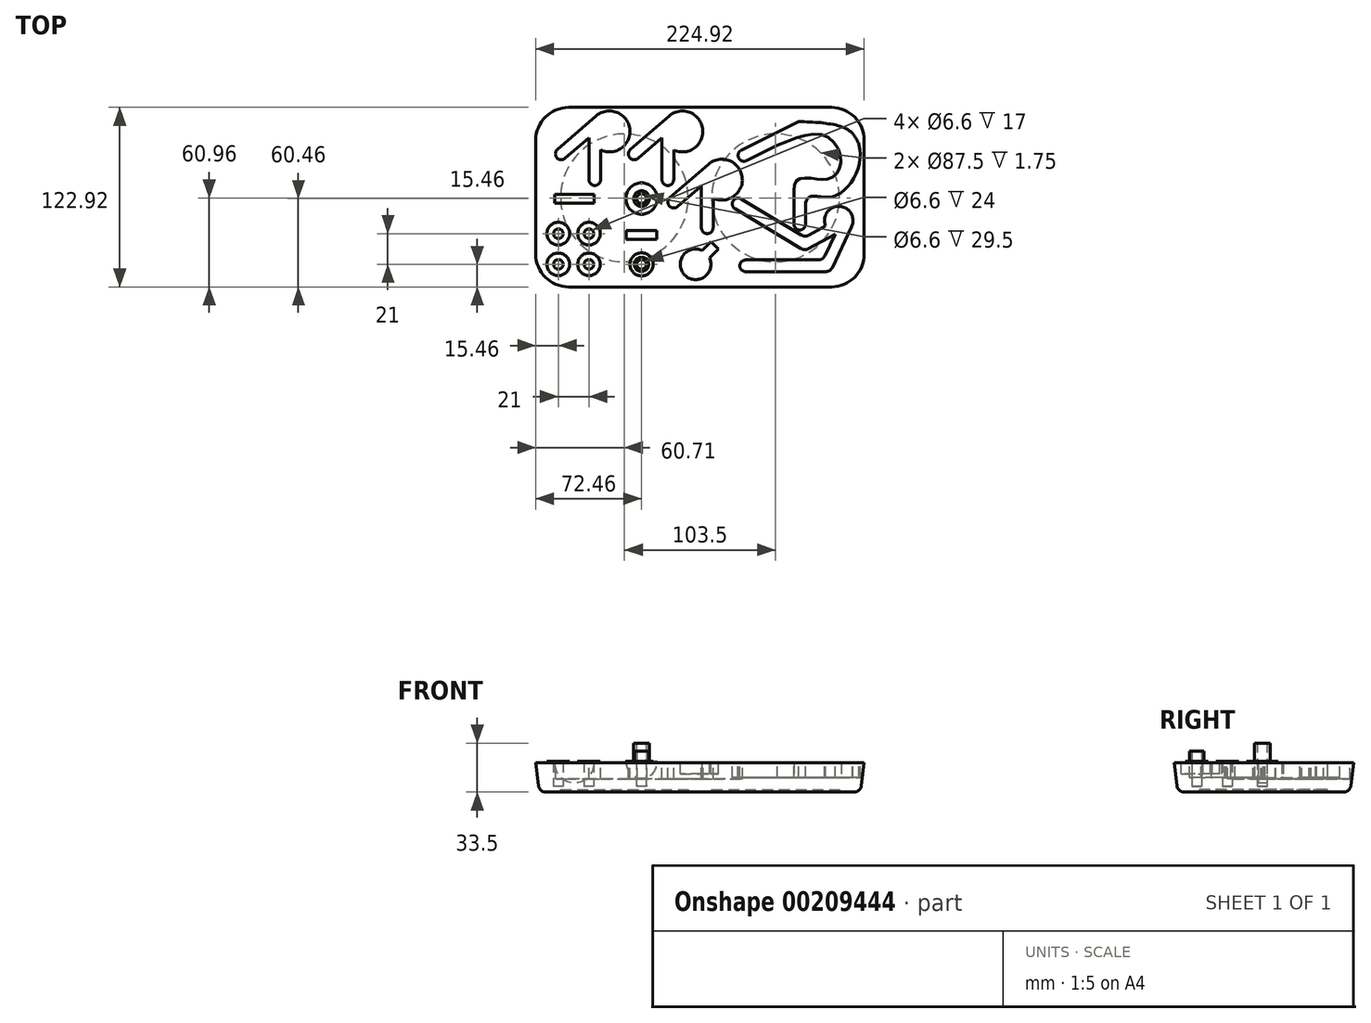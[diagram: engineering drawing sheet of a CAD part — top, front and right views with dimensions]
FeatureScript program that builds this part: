
annotation { "Feature Type Name" : "Feature", "Feature Type Description" : "" }
export const myFeature = defineFeature(function(context is Context, id is Id, definition is map)
    precondition{}
    {
        {
            var Q0;
            Q0=qCreatedBy(makeId("Top.planeOp"),FACE);
            var sketch = newSketch(context, id + "F0", { "sketchPlane" : qUnion([Q0])});
            skLineSegment(sketch, "E0.bottom", {"start": v(20, 0) * mm, "end": v(200, 0) * mm});
            skLineSegment(sketch, "E0.top", {"start": v(20, 118) * mm, "end": v(200, 118) * mm});
            skLineSegment(sketch, "E0.left", {"start": v(0, 20) * mm, "end": v(0, 98) * mm});
            skLineSegment(sketch, "E0.right", {"start": v(220, 20) * mm, "end": v(220, 98) * mm});
            skPoint(sketch, "E1.visualSharp", {"position": v(0, 118) * mm});
            skArc(sketch, "E1.filletArc", {"start": v(20, 118) * mm, "mid": v(5.86, 112.14) * mm, "end": v(0, 98) * mm});
            skPoint(sketch, "E2.visualSharp", {"position": v(220, 118) * mm});
            skArc(sketch, "E2.filletArc", {"start": v(220, 98) * mm, "mid": v(214.14, 112.14) * mm, "end": v(200, 118) * mm});
            skPoint(sketch, "E3.visualSharp", {"position": v(0, 0) * mm});
            skArc(sketch, "E3.filletArc", {"start": v(0, 20) * mm, "mid": v(5.86, 5.86) * mm, "end": v(20, 0) * mm});
            skPoint(sketch, "E4.visualSharp", {"position": v(220, 0) * mm});
            skArc(sketch, "E4.filletArc", {"start": v(200, 0) * mm, "mid": v(214.14, 5.86) * mm, "end": v(220, 20) * mm});
            skSolve(sketch);
        }
        {
            var Q0;
            Q0=makeQuery(id+"F0.imprint","IMPRINT",FACE,{"disambiguationData":[TD([[makeQuery(id+"F0.imprint","IMPRINT",EDGE,{"derivedFrom":sQuery(id+"F0.wireOp",EDGE,"E0.bottom")}),1.0]])]});
            extrude(context, id + "F1", {"entities" : qUnion([Q0]), "depth" : 20 * mm, "hasDraft" : true, "draftAngle" : 7 * degree});
        }
        {
            var Q0;
            Q0=makeQuery(id+"F1.opExtrude","CAP_FACE",FACE,{"disambiguationData":[OSD([sQuery(id+"F0.wireOp",EDGE,"E0.bottom"),sQuery(id+"F0.wireOp",EDGE,"E0.top"),sQuery(id+"F0.wireOp",EDGE,"E0.left"),sQuery(id+"F0.wireOp",EDGE,"E0.right"),sQuery(id+"F0.wireOp",EDGE,"E1.filletArc"),sQuery(id+"F0.wireOp",EDGE,"E2.filletArc"),sQuery(id+"F0.wireOp",EDGE,"E3.filletArc"),sQuery(id+"F0.wireOp",EDGE,"E4.filletArc")])],"isStart":true});
            fillet(context, id + "F2", {"entities" : qUnion([Q0]), "radius" : 5 * mm, "tangentPropagation" : true, "allowEdgeOverflow" : false});
        }
        {
            var Q0;
            Q0=makeQuery(id+"F1.opExtrude","CAP_FACE",FACE,{"disambiguationData":[OSD([sQuery(id+"F0.wireOp",EDGE,"E0.bottom"),sQuery(id+"F0.wireOp",EDGE,"E0.top"),sQuery(id+"F0.wireOp",EDGE,"E0.left"),sQuery(id+"F0.wireOp",EDGE,"E0.right"),sQuery(id+"F0.wireOp",EDGE,"E1.filletArc"),sQuery(id+"F0.wireOp",EDGE,"E2.filletArc"),sQuery(id+"F0.wireOp",EDGE,"E3.filletArc"),sQuery(id+"F0.wireOp",EDGE,"E4.filletArc")])],"isStart":true});
            var sketch = newSketch(context, id + "F3", { "sketchPlane" : qUnion([Q0])});
            skLineSegment(sketch, "E5.bottom", {"start": v(0, 0) * mm, "end": v(58.25, 0) * mm, "construction": true});
            skLineSegment(sketch, "E5.top", {"start": v(0, -58.5) * mm, "end": v(58.25, -58.5) * mm, "construction": true});
            skLineSegment(sketch, "E5.left", {"start": v(0, 0) * mm, "end": v(0, -58.5) * mm, "construction": true});
            skLineSegment(sketch, "E5.right", {"start": v(58.25, 0) * mm, "end": v(58.25, -58.5) * mm, "construction": true});
            skLineSegment(sketch, "E6.bottom", {"start": v(0, 0) * mm, "end": v(161.75, 0) * mm, "construction": true});
            skLineSegment(sketch, "E6.top", {"start": v(0, -58.5) * mm, "end": v(161.75, -58.5) * mm, "construction": true});
            skLineSegment(sketch, "E6.right", {"start": v(161.75, 0) * mm, "end": v(161.75, -58.5) * mm, "construction": true});
            skCircle(sketch, "E7", {"center": v(58.25, -58.5) * mm, "radius": 43.75 * mm});
            skCircle(sketch, "E8", {"center": v(161.75, -58.5) * mm, "radius": 43.75 * mm});
            skSolve(sketch);
        }
        {
            var Q0;
            Q0=qSketchRegion(id+"F3",true);
            extrude(context, id + "F4", {"entities" : qUnion([Q0]), "operationType" : NewBodyOperationType.REMOVE, "oppositeDirection" : true, "depth" : 1.75 * mm});
        }
        {
            var Q0;
            Q0=makeQuery(id+"F1.opExtrude","CAP_FACE",FACE,{"disambiguationData":[OSD([sQuery(id+"F0.wireOp",EDGE,"E0.bottom"),sQuery(id+"F0.wireOp",EDGE,"E0.top"),sQuery(id+"F0.wireOp",EDGE,"E0.left"),sQuery(id+"F0.wireOp",EDGE,"E0.right"),sQuery(id+"F0.wireOp",EDGE,"E1.filletArc"),sQuery(id+"F0.wireOp",EDGE,"E2.filletArc"),sQuery(id+"F0.wireOp",EDGE,"E3.filletArc"),sQuery(id+"F0.wireOp",EDGE,"E4.filletArc")])],"isStart":false});
            var sketch = newSketch(context, id + "F5", { "sketchPlane" : qUnion([Q0])});
            skLineSegment(sketch, "E9.bottom", {"start": v(0, 0) * mm, "end": v(205, 0) * mm, "construction": true});
            skLineSegment(sketch, "E9.top", {"start": v(0, 43) * mm, "end": v(205, 43) * mm, "construction": true});
            skLineSegment(sketch, "E9.left", {"start": v(0, 0) * mm, "end": v(0, 43) * mm, "construction": true});
            skLineSegment(sketch, "E9.right", {"start": v(205, 0) * mm, "end": v(205, 43) * mm, "construction": true});
            skArc(sketch, "E10", {"start": v(213.81, 38.83) * mm, "mid": v(205.19, 52.75) * mm, "end": v(196.03, 39.18) * mm});
            skLineSegment(sketch, "E11", {"start": v(213.81, 38.83) * mm, "end": v(200.6, 10.86) * mm});
            skLineSegment(sketch, "E12", {"start": v(196.07, 8) * mm, "end": v(141.24, 8) * mm});
            skLineSegment(sketch, "E13", {"start": v(137.24, 12) * mm, "end": v(137.24, 12) * mm});
            skLineSegment(sketch, "E14", {"start": v(141.24, 16) * mm, "end": v(191, 16) * mm});
            skPoint(sketch, "E15.visualSharp", {"position": v(194.17, 16) * mm});
            skArc(sketch, "E15.filletArc", {"start": v(191, 16) * mm, "mid": v(193.68, 16.78) * mm, "end": v(195.53, 18.86) * mm});
            skPoint(sketch, "E16.visualSharp", {"position": v(199.24, 8) * mm});
            skArc(sketch, "E16.filletArc", {"start": v(196.07, 8) * mm, "mid": v(198.75, 8.78) * mm, "end": v(200.6, 10.86) * mm});
            skPoint(sketch, "E17.visualSharp", {"position": v(137.24, 16) * mm});
            skArc(sketch, "E17.filletArc", {"start": v(141.24, 16) * mm, "mid": v(138.41, 14.83) * mm, "end": v(137.24, 12) * mm});
            skPoint(sketch, "E18.visualSharp", {"position": v(137.24, 8) * mm});
            skArc(sketch, "E18.filletArc", {"start": v(137.24, 12) * mm, "mid": v(138.41, 9.17) * mm, "end": v(141.24, 8) * mm});
            skLineSegment(sketch, "E19.trimOffspring", {"start": v(202.48, 33.58) * mm, "end": v(195.53, 18.86) * mm});
            skLineSegment(sketch, "E20", {"start": v(196.03, 39.18) * mm, "end": v(184.43, 32.88) * mm});
            skLineSegment(sketch, "E21", {"start": v(179.46, 32.99) * mm, "end": v(138.25, 57.86) * mm});
            skLineSegment(sketch, "E22", {"start": v(132.76, 56.5) * mm, "end": v(132.76, 56.5) * mm});
            skLineSegment(sketch, "E23", {"start": v(134.12, 51.01) * mm, "end": v(179.25, 23.77) * mm});
            skLineSegment(sketch, "E24", {"start": v(202.48, 33.58) * mm, "end": v(184.22, 23.66) * mm});
            skPoint(sketch, "E25.visualSharp", {"position": v(181.7, 22.3) * mm});
            skArc(sketch, "E25.filletArc", {"start": v(179.25, 23.77) * mm, "mid": v(181.72, 23.05) * mm, "end": v(184.22, 23.66) * mm});
            skPoint(sketch, "E26.visualSharp", {"position": v(181.91, 31.5) * mm});
            skArc(sketch, "E26.filletArc", {"start": v(179.46, 32.99) * mm, "mid": v(181.93, 32.27) * mm, "end": v(184.43, 32.88) * mm});
            skPoint(sketch, "E27.visualSharp", {"position": v(134.82, 59.93) * mm});
            skArc(sketch, "E27.filletArc", {"start": v(138.25, 57.86) * mm, "mid": v(135.22, 58.32) * mm, "end": v(132.76, 56.5) * mm});
            skPoint(sketch, "E28.visualSharp", {"position": v(130.7, 53.08) * mm});
            skArc(sketch, "E28.filletArc", {"start": v(132.76, 56.5) * mm, "mid": v(132.3, 53.48) * mm, "end": v(134.12, 51.01) * mm});
            skLineSegment(sketch, "E29.bottom", {"start": v(0, 0) * mm, "end": v(191, 0) * mm, "construction": true});
            skLineSegment(sketch, "E29.top", {"start": v(0, 84) * mm, "end": v(191, 84) * mm, "construction": true});
            skLineSegment(sketch, "E29.left", {"start": v(0, 0) * mm, "end": v(0, 84) * mm, "construction": true});
            skLineSegment(sketch, "E29.right", {"start": v(191, 0) * mm, "end": v(191, 84) * mm, "construction": true});
            skLineSegment(sketch, "E30", {"start": v(177.57, 110.83) * mm, "end": v(138.3, 91.17) * mm});
            skLineSegment(sketch, "E31", {"start": v(136.52, 85.8) * mm, "end": v(136.52, 85.8) * mm});
            skLineSegment(sketch, "E32", {"start": v(141.88, 84.01) * mm, "end": v(162.91, 94.54) * mm});
            skPoint(sketch, "E33.visualSharp", {"position": v(174.15, 39.17) * mm});
            skPoint(sketch, "E34.visualSharp", {"position": v(182.15, 39.17) * mm});
            skPoint(sketch, "E35.visualSharp", {"position": v(138.3, 82.22) * mm});
            skArc(sketch, "E35.filletArc", {"start": v(136.52, 85.8) * mm, "mid": v(138.83, 83.8) * mm, "end": v(141.88, 84.01) * mm});
            skPoint(sketch, "E36.visualSharp", {"position": v(134.73, 89.38) * mm});
            skArc(sketch, "E36.filletArc", {"start": v(138.3, 91.17) * mm, "mid": v(136.3, 88.85) * mm, "end": v(136.52, 85.8) * mm});
            skArc(sketch, "E37", {"start": v(174.32, 40.48) * mm, "mid": v(178.32, 36.48) * mm, "end": v(182.32, 40.48) * mm});
            skLineSegment(sketch, "E38", {"start": v(182.32, 55.28) * mm, "end": v(182.32, 40.48) * mm});
            skLineSegment(sketch, "E39", {"start": v(174.32, 59.6) * mm, "end": v(174.32, 40.48) * mm});
            skFitSpline(sketch, "E40", {"points": [v(174.32, 59.6) * mm, v(176.31, 70.54) * mm, v(187.5, 71.78) * mm, v(199.68, 72.28) * mm, v(206.63, 83.7) * mm, v(195.45, 101.1) * mm, v(162.91, 94.54) * mm], "startDerivative": vector(-2.68, 96.5) * mm, "endDerivative": vector(-150.94, -63.2) * mm});
            skFitSpline(sketch, "E41", {"points": [v(182.32, 55.28) * mm, v(185.68, 59.44) * mm, v(200.84, 59.44) * mm, v(218.24, 78.83) * mm, v(214.35, 102.83) * mm, v(177.57, 110.83) * mm], "startDerivative": vector(21.88, 51.8) * mm, "endDerivative": vector(-161.72, 6.15) * mm});
            skArc(sketch, "E42.trimOffspring", {"start": v(218.92, 94.98) * mm, "mid": v(201.73, 112.01) * mm, "end": v(177.57, 110.83) * mm});
            skSolve(sketch);
        }
        {
            var Q0;
            Q0=makeQuery(id+"F5.imprint","IMPRINT",FACE,{"disambiguationData":[TD([[makeQuery(id+"F5.imprint","IMPRINT",EDGE,{"derivedFrom":sQuery(id+"F5.wireOp",EDGE,"E30")}),1.0]])]});
            var Q1;
            Q1=makeQuery(id+"F5.imprint","IMPRINT",FACE,{"disambiguationData":[TD([[makeQuery(id+"F5.imprint","IMPRINT",EDGE,{"derivedFrom":sQuery(id+"F5.wireOp",EDGE,"E10")}),1.0]])]});
            extrude(context, id + "F6", {"entities" : qUnion([Q0, Q1]), "operationType" : NewBodyOperationType.REMOVE, "oppositeDirection" : true, "depth" : 10 * mm});
        }
        {
            var Q0;
            Q0=makeQuery(id+"F1.opExtrude","CAP_FACE",FACE,{"disambiguationData":[OSD([sQuery(id+"F0.wireOp",EDGE,"E0.bottom"),sQuery(id+"F0.wireOp",EDGE,"E0.top"),sQuery(id+"F0.wireOp",EDGE,"E0.left"),sQuery(id+"F0.wireOp",EDGE,"E0.right"),sQuery(id+"F0.wireOp",EDGE,"E1.filletArc"),sQuery(id+"F0.wireOp",EDGE,"E2.filletArc"),sQuery(id+"F0.wireOp",EDGE,"E3.filletArc"),sQuery(id+"F0.wireOp",EDGE,"E4.filletArc")])],"isStart":false});
            var sketch = newSketch(context, id + "F7", { "sketchPlane" : qUnion([Q0])});
            skLineSegment(sketch, "E43.bottom", {"start": v(0, 0) * mm, "end": v(13, 0) * mm, "construction": true});
            skLineSegment(sketch, "E43.top", {"start": v(0, 13) * mm, "end": v(13, 13) * mm, "construction": true});
            skLineSegment(sketch, "E43.left", {"start": v(0, 0) * mm, "end": v(0, 13) * mm, "construction": true});
            skLineSegment(sketch, "E43.right", {"start": v(13, 0) * mm, "end": v(13, 13) * mm, "construction": true});
            skLineSegment(sketch, "E44.bottom", {"start": v(13, 13) * mm, "end": v(34, 13) * mm, "construction": true});
            skLineSegment(sketch, "E44.top", {"start": v(13, 34) * mm, "end": v(34, 34) * mm, "construction": true});
            skLineSegment(sketch, "E44.left", {"start": v(13, 13) * mm, "end": v(13, 34) * mm, "construction": true});
            skLineSegment(sketch, "E44.right", {"start": v(34, 13) * mm, "end": v(34, 34) * mm, "construction": true});
            skCircle(sketch, "E45", {"center": v(13, 34) * mm, "radius": 7.75 * mm});
            skCircle(sketch, "E46", {"center": v(34, 34) * mm, "radius": 7.75 * mm});
            skCircle(sketch, "E47", {"center": v(34, 13) * mm, "radius": 7.75 * mm});
            skCircle(sketch, "E48", {"center": v(13, 13) * mm, "radius": 7.75 * mm});
            skCircle(sketch, "E49", {"center": v(34, 34) * mm, "radius": 3.3 * mm});
            skCircle(sketch, "E50", {"center": v(34, 13) * mm, "radius": 3.3 * mm});
            skCircle(sketch, "E51", {"center": v(13, 13) * mm, "radius": 3.3 * mm});
            skCircle(sketch, "E52", {"center": v(13, 34) * mm, "radius": 3.3 * mm});
            skSolve(sketch);
        }
        {
            var Q0;
            Q0 = qSketchRegion(id + "F7", true);
            extrude(context, id + "F8", {"entities" : qUnion([Q0]), "operationType" : NewBodyOperationType.ADD, "depth" : 1 * mm});
        }
        {
            var Q0;
            Q0=makeQuery(id+"F7.imprint","IMPRINT",FACE,{"disambiguationData":[TD([[makeQuery(id+"F7.imprint","IMPRINT",EDGE,{"derivedFrom":sQuery(id+"F7.wireOp",EDGE,"E52")}),1.0]])]});
            var Q1;
            Q1=makeQuery(id+"F7.imprint","IMPRINT",FACE,{"disambiguationData":[TD([[makeQuery(id+"F7.imprint","IMPRINT",EDGE,{"derivedFrom":sQuery(id+"F7.wireOp",EDGE,"E49")}),1.0]])]});
            var Q2;
            Q2=makeQuery(id+"F7.imprint","IMPRINT",FACE,{"disambiguationData":[TD([[makeQuery(id+"F7.imprint","IMPRINT",EDGE,{"derivedFrom":sQuery(id+"F7.wireOp",EDGE,"E50")}),1.0]])]});
            var Q3;
            Q3=makeQuery(id+"F7.imprint","IMPRINT",FACE,{"disambiguationData":[TD([[makeQuery(id+"F7.imprint","IMPRINT",EDGE,{"derivedFrom":sQuery(id+"F7.wireOp",EDGE,"E51")}),1.0]])]});
            extrude(context, id + "F9", {"entities" : qUnion([Q0, Q1, Q2, Q3]), "operationType" : NewBodyOperationType.REMOVE, "oppositeDirection" : true, "depth" : 16 * mm});
        }
        {
            var Q0;
            {var subQ0=sQuery(id+"F0.wireOp",EDGE,"E0.bottom");var subQ1=sQuery(id+"F0.wireOp",EDGE,"E2.filletArc");var subQ2=sQuery(id+"F0.wireOp",EDGE,"E0.right");var subQ3=sQuery(id+"F0.wireOp",EDGE,"E0.left");var subQ4=sQuery(id+"F0.wireOp",EDGE,"E0.top");var subQ5=sQuery(id+"F0.wireOp",EDGE,"E1.filletArc");var subQ6=sQuery(id+"F0.wireOp",EDGE,"E3.filletArc");var subQ7=sQuery(id+"F0.wireOp",EDGE,"E4.filletArc");Q0=makeQuery(id+"F8.boolean.opBoolean","SPLIT",FACE,{"disambiguationData":[TD([makeQuery(id+"F1.opExtrude","SWEPT_FACE",FACE,{"disambiguationData":[OSD([subQ0])]})])],"derivedFrom":makeQuery(id+"F1.opExtrude","CAP_FACE",FACE,{"disambiguationData":[OSD([subQ0,subQ4,subQ3,subQ2,subQ5,subQ1,subQ6,subQ7])],"isStart":false})});}
            var sketch = newSketch(context, id + "F10", { "sketchPlane" : qUnion([Q0])});
            skLineSegment(sketch, "E53.bottom", {"start": v(0, 0) * mm, "end": v(24, 0) * mm, "construction": true});
            skLineSegment(sketch, "E53.top", {"start": v(0, 55) * mm, "end": v(24, 55) * mm, "construction": true});
            skLineSegment(sketch, "E53.left", {"start": v(0, 0) * mm, "end": v(0, 55) * mm, "construction": true});
            skLineSegment(sketch, "E53.right", {"start": v(24, 0) * mm, "end": v(24, 55) * mm, "construction": true});
            skLineSegment(sketch, "E54.bottom", {"start": v(24, 55) * mm, "end": v(37.5, 55) * mm});
            skLineSegment(sketch, "E54.top", {"start": v(24, 61) * mm, "end": v(37.5, 61) * mm});
            skLineSegment(sketch, "E54.left", {"start": v(24, 55) * mm, "end": v(24, 61) * mm});
            skLineSegment(sketch, "E54.right", {"start": v(37.5, 55) * mm, "end": v(37.5, 61) * mm});
            skSolve(sketch);
        }
        {
            var Q0;
            Q0=makeQuery(id+"F10.imprint","IMPRINT",FACE,{"disambiguationData":[TD([[makeQuery(id+"F10.imprint","IMPRINT",EDGE,{"derivedFrom":sQuery(id+"F10.wireOp",EDGE,"E54.bottom")}),1.0]])]});
            var Q1;
            Q1=sQuery(id+"F10.wireOp",EDGE,"E54.left");
            revolve(context, id + "F11", {"operationType" : NewBodyOperationType.REMOVE, "entities" : qUnion([Q0]), "axis" : qUnion([Q1]), "revolveType" : RevolveType.FULL, "oppositeDirection" : true});
        }
        {
            var Q0;
            {var subQ0=sQuery(id+"F0.wireOp",EDGE,"E0.bottom");var subQ1=sQuery(id+"F0.wireOp",EDGE,"E2.filletArc");var subQ2=sQuery(id+"F0.wireOp",EDGE,"E0.right");var subQ3=sQuery(id+"F0.wireOp",EDGE,"E0.left");var subQ4=sQuery(id+"F0.wireOp",EDGE,"E0.top");var subQ5=sQuery(id+"F0.wireOp",EDGE,"E1.filletArc");var subQ6=sQuery(id+"F0.wireOp",EDGE,"E3.filletArc");var subQ7=sQuery(id+"F0.wireOp",EDGE,"E4.filletArc");Q0=makeQuery(id+"F8.boolean.opBoolean","SPLIT",FACE,{"disambiguationData":[TD([makeQuery(id+"F1.opExtrude","SWEPT_FACE",FACE,{"disambiguationData":[OSD([subQ0])]})])],"derivedFrom":makeQuery(id+"F1.opExtrude","CAP_FACE",FACE,{"disambiguationData":[OSD([subQ0,subQ4,subQ3,subQ2,subQ5,subQ1,subQ6,subQ7])],"isStart":false})});}
            var sketch = newSketch(context, id + "F12", { "sketchPlane" : qUnion([Q0])});
            skLineSegment(sketch, "E55.bottom", {"start": v(0, 0) * mm, "end": v(70, 0) * mm, "construction": true});
            skLineSegment(sketch, "E55.top", {"start": v(0, 58) * mm, "end": v(70, 58) * mm, "construction": true});
            skLineSegment(sketch, "E55.left", {"start": v(0, 0) * mm, "end": v(0, 58) * mm, "construction": true});
            skLineSegment(sketch, "E55.right", {"start": v(70, 0) * mm, "end": v(70, 58) * mm, "construction": true});
            skCircle(sketch, "E56", {"center": v(70, 58) * mm, "radius": 5.35 * mm});
            skCircle(sketch, "E57", {"center": v(70, 58) * mm, "radius": 3.3 * mm});
            skCircle(sketch, "E58", {"center": v(70, 58) * mm, "radius": 10.75 * mm});
            skLineSegment(sketch, "E59.top", {"start": v(0, 13) * mm, "end": v(70, 13) * mm, "construction": true});
            skLineSegment(sketch, "E59.left", {"start": v(0, 0) * mm, "end": v(0, 13) * mm, "construction": true});
            skLineSegment(sketch, "E59.right", {"start": v(70, 0) * mm, "end": v(70, 13) * mm, "construction": true});
            skCircle(sketch, "E60", {"center": v(70, 13) * mm, "radius": 3.3 * mm});
            skCircle(sketch, "E61", {"center": v(70, 13) * mm, "radius": 7.9 * mm});
            skCircle(sketch, "E62", {"center": v(70, 13) * mm, "radius": 4.9 * mm});
            skSolve(sketch);
        }
        {
            var Q0;
            Q0=makeQuery(id+"F12.imprint","IMPRINT",FACE,{"disambiguationData":[TD([[makeQuery(id+"F12.imprint","IMPRINT",EDGE,{"derivedFrom":sQuery(id+"F12.wireOp",EDGE,"E56")}),-1.0]])]});
            var Q1;
            Q1=makeQuery(id+"F12.imprint","IMPRINT",FACE,{"disambiguationData":[TD([[makeQuery(id+"F12.imprint","IMPRINT",EDGE,{"derivedFrom":sQuery(id+"F12.wireOp",EDGE,"E61")}),1.0]])]});
            extrude(context, id + "F13", {"entities" : qUnion([Q0, Q1]), "operationType" : NewBodyOperationType.ADD, "depth" : 1 * mm});
        }
        {
            var Q0;
            Q0=makeQuery(id+"F12.imprint","IMPRINT",FACE,{"disambiguationData":[TD([[makeQuery(id+"F12.imprint","IMPRINT",EDGE,{"derivedFrom":sQuery(id+"F12.wireOp",EDGE,"E60")}),-1.0]])]});
            extrude(context, id + "F14", {"entities" : qUnion([Q0]), "operationType" : NewBodyOperationType.ADD, "depth" : 8 * mm});
        }
        {
            var Q0;
            Q0=makeQuery(id+"F12.imprint","IMPRINT",FACE,{"disambiguationData":[TD([[makeQuery(id+"F12.imprint","IMPRINT",EDGE,{"derivedFrom":sQuery(id+"F12.wireOp",EDGE,"E57")}),1.0]])]});
            var Q1;
            Q1=makeQuery(id+"F12.imprint","IMPRINT",FACE,{"disambiguationData":[TD([[makeQuery(id+"F12.imprint","IMPRINT",EDGE,{"derivedFrom":sQuery(id+"F12.wireOp",EDGE,"E60")}),1.0]])]});
            extrude(context, id + "F15", {"entities" : qUnion([Q0, Q1]), "operationType" : NewBodyOperationType.REMOVE, "oppositeDirection" : true, "depth" : 16 * mm});
        }
        {
            var Q0;
            Q0=makeQuery(id+"F12.imprint","IMPRINT",FACE,{"disambiguationData":[TD([[makeQuery(id+"F12.imprint","IMPRINT",EDGE,{"derivedFrom":sQuery(id+"F12.wireOp",EDGE,"E56")}),1.0]])]});
            extrude(context, id + "F16", {"entities" : qUnion([Q0]), "operationType" : NewBodyOperationType.ADD, "depth" : 13.5 * mm});
        }
        {
            var Q0;
            {var subQ2=sQuery(id+"F0.wireOp",EDGE,"E0.bottom");var subQ3=makeQuery(id+"F1.opExtrude","SWEPT_FACE",FACE,{"disambiguationData":[OSD([subQ2])]});var subQ6=sQuery(id+"F0.wireOp",EDGE,"E2.filletArc");var subQ9=sQuery(id+"F0.wireOp",EDGE,"E0.right");var subQ18=sQuery(id+"F0.wireOp",EDGE,"E0.left");var subQ24=sQuery(id+"F0.wireOp",EDGE,"E0.top");var subQ27=sQuery(id+"F0.wireOp",EDGE,"E1.filletArc");var subQ32=sQuery(id+"F0.wireOp",EDGE,"E3.filletArc");var subQ34=sQuery(id+"F0.wireOp",EDGE,"E4.filletArc");Q0=makeQuery(id+"F13.boolean.opBoolean","SPLIT",FACE,{"disambiguationData":[TD([subQ3])],"derivedFrom":makeQuery(id+"F8.boolean.opBoolean","SPLIT",FACE,{"disambiguationData":[TD([subQ3])],"derivedFrom":makeQuery(id+"F1.opExtrude","CAP_FACE",FACE,{"disambiguationData":[OSD([subQ2,subQ24,subQ18,subQ9,subQ27,subQ6,subQ32,subQ34])],"isStart":false})})});}
            var sketch = newSketch(context, id + "F17", { "sketchPlane" : qUnion([Q0])});
            skLineSegment(sketch, "E63.bottom", {"start": v(0, 0) * mm, "end": v(70, 0) * mm, "construction": true});
            skLineSegment(sketch, "E63.top", {"start": v(0, 30) * mm, "end": v(70, 30) * mm, "construction": true});
            skLineSegment(sketch, "E63.left", {"start": v(0, 0) * mm, "end": v(0, 30) * mm, "construction": true});
            skLineSegment(sketch, "E63.right", {"start": v(70, 0) * mm, "end": v(70, 30) * mm, "construction": true});
            skLineSegment(sketch, "E64.bottom", {"start": v(70, 30) * mm, "end": v(80.5, 30) * mm});
            skLineSegment(sketch, "E64.top", {"start": v(70, 36) * mm, "end": v(80.5, 36) * mm});
            skLineSegment(sketch, "E64.left", {"start": v(70, 30) * mm, "end": v(70, 36) * mm});
            skLineSegment(sketch, "E64.right", {"start": v(80.5, 30) * mm, "end": v(80.5, 36) * mm});
            skSolve(sketch);
        }
        {
            var Q0;
            Q0 = qSketchRegion(id + "F17", true);
            var Q1;
            Q1=sQuery(id+"F17.wireOp",EDGE,"E64.left");
            revolve(context, id + "F18", {"operationType" : NewBodyOperationType.REMOVE, "entities" : qUnion([Q0]), "axis" : qUnion([Q1]), "revolveType" : RevolveType.FULL});
        }
        {
            var Q0;
            {var subQ2=sQuery(id+"F0.wireOp",EDGE,"E0.bottom");var subQ3=makeQuery(id+"F1.opExtrude","SWEPT_FACE",FACE,{"disambiguationData":[OSD([subQ2])]});var subQ6=sQuery(id+"F0.wireOp",EDGE,"E2.filletArc");var subQ9=sQuery(id+"F0.wireOp",EDGE,"E0.right");var subQ18=sQuery(id+"F0.wireOp",EDGE,"E0.left");var subQ24=sQuery(id+"F0.wireOp",EDGE,"E0.top");var subQ27=sQuery(id+"F0.wireOp",EDGE,"E1.filletArc");var subQ32=sQuery(id+"F0.wireOp",EDGE,"E3.filletArc");var subQ34=sQuery(id+"F0.wireOp",EDGE,"E4.filletArc");Q0=makeQuery(id+"F13.boolean.opBoolean","SPLIT",FACE,{"disambiguationData":[TD([subQ3])],"derivedFrom":makeQuery(id+"F8.boolean.opBoolean","SPLIT",FACE,{"disambiguationData":[TD([subQ3])],"derivedFrom":makeQuery(id+"F1.opExtrude","CAP_FACE",FACE,{"disambiguationData":[OSD([subQ2,subQ24,subQ18,subQ9,subQ27,subQ6,subQ32,subQ34])],"isStart":false})})});}
            var sketch = newSketch(context, id + "F19", { "sketchPlane" : qUnion([Q0])});
            skLineSegment(sketch, "E65.bottom", {"start": v(0, 0) * mm, "end": v(107, 0) * mm, "construction": true});
            skLineSegment(sketch, "E65.top", {"start": v(0, 13) * mm, "end": v(107, 13) * mm, "construction": true});
            skLineSegment(sketch, "E65.left", {"start": v(0, 0) * mm, "end": v(0, 13) * mm, "construction": true});
            skLineSegment(sketch, "E65.right", {"start": v(107, 0) * mm, "end": v(107, 13) * mm, "construction": true});
            skArc(sketch, "E66", {"start": v(111.43, 22.52) * mm, "mid": v(99.58, 5.58) * mm, "end": v(116.52, 17.43) * mm});
            skLineSegment(sketch, "E67", {"start": v(107, 13) * mm, "end": v(120.06, 26.06) * mm, "construction": true});
            skLineSegment(sketch, "E68", {"start": v(120.06, 26.06) * mm, "end": v(122.6, 23.52) * mm});
            skLineSegment(sketch, "E69", {"start": v(122.6, 23.52) * mm, "end": v(116.52, 17.43) * mm});
            skLineSegment(sketch, "E70", {"start": v(120.06, 26.06) * mm, "end": v(117.52, 28.6) * mm});
            skLineSegment(sketch, "E71", {"start": v(117.52, 28.6) * mm, "end": v(111.43, 22.52) * mm});
            skSolve(sketch);
        }
        {
            var Q0;
            Q0=makeQuery(id+"F19.imprint","IMPRINT",FACE,{"disambiguationData":[TD([[makeQuery(id+"F19.imprint","IMPRINT",EDGE,{"derivedFrom":sQuery(id+"F19.wireOp",EDGE,"E66")}),1.0]])]});
            extrude(context, id + "F20", {"entities" : qUnion([Q0]), "operationType" : NewBodyOperationType.REMOVE, "oppositeDirection" : true, "depth" : 7.5 * mm});
        }
        {
            var Q0;
            {var subQ2=sQuery(id+"F0.wireOp",EDGE,"E0.bottom");var subQ3=makeQuery(id+"F1.opExtrude","SWEPT_FACE",FACE,{"disambiguationData":[OSD([subQ2])]});var subQ6=sQuery(id+"F0.wireOp",EDGE,"E2.filletArc");var subQ9=sQuery(id+"F0.wireOp",EDGE,"E0.right");var subQ18=sQuery(id+"F0.wireOp",EDGE,"E0.left");var subQ24=sQuery(id+"F0.wireOp",EDGE,"E0.top");var subQ27=sQuery(id+"F0.wireOp",EDGE,"E1.filletArc");var subQ32=sQuery(id+"F0.wireOp",EDGE,"E3.filletArc");var subQ34=sQuery(id+"F0.wireOp",EDGE,"E4.filletArc");Q0=makeQuery(id+"F13.boolean.opBoolean","SPLIT",FACE,{"disambiguationData":[TD([subQ3])],"derivedFrom":makeQuery(id+"F8.boolean.opBoolean","SPLIT",FACE,{"disambiguationData":[TD([subQ3])],"derivedFrom":makeQuery(id+"F1.opExtrude","CAP_FACE",FACE,{"disambiguationData":[OSD([subQ2,subQ24,subQ18,subQ9,subQ27,subQ6,subQ32,subQ34])],"isStart":false})})});}
            var sketch = newSketch(context, id + "F21", { "sketchPlane" : qUnion([Q0])});
            skLineSegment(sketch, "E72.bottom", {"start": v(0, 0) * mm, "end": v(125, 0) * mm, "construction": true});
            skLineSegment(sketch, "E72.top", {"start": v(0, 71) * mm, "end": v(125, 71) * mm, "construction": true});
            skLineSegment(sketch, "E72.left", {"start": v(0, 0) * mm, "end": v(0, 71) * mm, "construction": true});
            skLineSegment(sketch, "E72.right", {"start": v(125, 0) * mm, "end": v(125, 71) * mm, "construction": true});
            skArc(sketch, "E73", {"start": v(119, 58.35) * mm, "mid": v(138.87, 72.9) * mm, "end": v(115.82, 81.57) * mm});
            skLineSegment(sketch, "E74", {"start": v(111, 66.78) * mm, "end": v(111, 38) * mm});
            skLineSegment(sketch, "E75", {"start": v(115, 34) * mm, "end": v(115, 34) * mm});
            skLineSegment(sketch, "E76", {"start": v(119, 38) * mm, "end": v(119, 58.35) * mm});
            skLineSegment(sketch, "E77", {"start": v(115.82, 81.57) * mm, "end": v(89.4, 58.6) * mm});
            skLineSegment(sketch, "E78", {"start": v(89, 52.96) * mm, "end": v(89, 52.96) * mm});
            skLineSegment(sketch, "E79", {"start": v(94.65, 52.57) * mm, "end": v(111, 66.78) * mm});
            skLineSegment(sketch, "E80.bottom", {"start": v(0, 0) * mm, "end": v(98, 0) * mm, "construction": true});
            skLineSegment(sketch, "E80.top", {"start": v(0, 104) * mm, "end": v(98, 104) * mm, "construction": true});
            skLineSegment(sketch, "E80.left", {"start": v(0, 0) * mm, "end": v(0, 104) * mm, "construction": true});
            skLineSegment(sketch, "E80.right", {"start": v(98, 0) * mm, "end": v(98, 104) * mm, "construction": true});
            skArc(sketch, "E81", {"start": v(92, 91.35) * mm, "mid": v(111.87, 105.9) * mm, "end": v(88.82, 114.57) * mm});
            skLineSegment(sketch, "E82", {"start": v(84, 99.78) * mm, "end": v(84, 71) * mm});
            skLineSegment(sketch, "E83", {"start": v(88, 67) * mm, "end": v(88, 67) * mm});
            skLineSegment(sketch, "E84", {"start": v(92, 71) * mm, "end": v(92, 91.35) * mm});
            skLineSegment(sketch, "E85", {"start": v(88.82, 114.57) * mm, "end": v(62.4, 91.6) * mm});
            skLineSegment(sketch, "E86", {"start": v(62, 85.96) * mm, "end": v(62, 85.96) * mm});
            skLineSegment(sketch, "E87", {"start": v(67.65, 85.57) * mm, "end": v(84, 99.78) * mm});
            skLineSegment(sketch, "E88.bottom", {"start": v(0, 0) * mm, "end": v(48, 0) * mm, "construction": true});
            skLineSegment(sketch, "E88.top", {"start": v(0, 104) * mm, "end": v(48, 104) * mm, "construction": true});
            skLineSegment(sketch, "E88.right", {"start": v(48, 0) * mm, "end": v(48, 104) * mm, "construction": true});
            skArc(sketch, "E89", {"start": v(42, 91.35) * mm, "mid": v(61.87, 105.9) * mm, "end": v(38.82, 114.57) * mm});
            skLineSegment(sketch, "E90", {"start": v(38.82, 114.57) * mm, "end": v(12.4, 91.6) * mm});
            skLineSegment(sketch, "E91", {"start": v(34, 99.78) * mm, "end": v(34, 71) * mm});
            skLineSegment(sketch, "E92", {"start": v(38, 67) * mm, "end": v(38, 67) * mm});
            skLineSegment(sketch, "E93", {"start": v(42, 71) * mm, "end": v(42, 91.35) * mm});
            skLineSegment(sketch, "E94", {"start": v(12, 85.96) * mm, "end": v(12, 85.96) * mm});
            skLineSegment(sketch, "E95", {"start": v(17.65, 85.57) * mm, "end": v(34, 99.78) * mm});
            skPoint(sketch, "E96.visualSharp", {"position": v(9.38, 88.98) * mm});
            skArc(sketch, "E96.filletArc", {"start": v(12.4, 91.6) * mm, "mid": v(11.03, 88.86) * mm, "end": v(12, 85.96) * mm});
            skPoint(sketch, "E97.visualSharp", {"position": v(14.63, 82.94) * mm});
            skArc(sketch, "E97.filletArc", {"start": v(12, 85.96) * mm, "mid": v(14.75, 84.6) * mm, "end": v(17.65, 85.57) * mm});
            skPoint(sketch, "E98.visualSharp", {"position": v(34, 67) * mm});
            skArc(sketch, "E98.filletArc", {"start": v(34, 71) * mm, "mid": v(35.17, 68.17) * mm, "end": v(38, 67) * mm});
            skPoint(sketch, "E99.visualSharp", {"position": v(84, 67) * mm});
            skArc(sketch, "E99.filletArc", {"start": v(84, 71) * mm, "mid": v(85.17, 68.17) * mm, "end": v(88, 67) * mm});
            skPoint(sketch, "E100.visualSharp", {"position": v(42, 67) * mm});
            skArc(sketch, "E100.filletArc", {"start": v(38, 67) * mm, "mid": v(40.83, 68.17) * mm, "end": v(42, 71) * mm});
            skPoint(sketch, "E101.visualSharp", {"position": v(119, 34) * mm});
            skArc(sketch, "E101.filletArc", {"start": v(115, 34) * mm, "mid": v(117.83, 35.17) * mm, "end": v(119, 38) * mm});
            skPoint(sketch, "E102.visualSharp", {"position": v(92, 67) * mm});
            skArc(sketch, "E102.filletArc", {"start": v(88, 67) * mm, "mid": v(90.83, 68.17) * mm, "end": v(92, 71) * mm});
            skPoint(sketch, "E103.visualSharp", {"position": v(59.38, 88.98) * mm});
            skArc(sketch, "E103.filletArc", {"start": v(62.4, 91.6) * mm, "mid": v(61.03, 88.86) * mm, "end": v(62, 85.96) * mm});
            skPoint(sketch, "E104.visualSharp", {"position": v(111, 34) * mm});
            skArc(sketch, "E104.filletArc", {"start": v(111, 38) * mm, "mid": v(112.17, 35.17) * mm, "end": v(115, 34) * mm});
            skPoint(sketch, "E105.visualSharp", {"position": v(91.63, 49.94) * mm});
            skArc(sketch, "E105.filletArc", {"start": v(89, 52.96) * mm, "mid": v(91.75, 51.6) * mm, "end": v(94.65, 52.57) * mm});
            skPoint(sketch, "E106.visualSharp", {"position": v(64.63, 82.94) * mm});
            skArc(sketch, "E106.filletArc", {"start": v(62, 85.96) * mm, "mid": v(64.75, 84.6) * mm, "end": v(67.65, 85.57) * mm});
            skPoint(sketch, "E107.visualSharp", {"position": v(86.38, 55.98) * mm});
            skArc(sketch, "E107.filletArc", {"start": v(89.4, 58.6) * mm, "mid": v(88.03, 55.86) * mm, "end": v(89, 52.96) * mm});
            skSolve(sketch);
        }
        {
            var Q0;
            Q0 = qSketchRegion(id + "F21", true);
            extrude(context, id + "F22", {"entities" : qUnion([Q0]), "operationType" : NewBodyOperationType.REMOVE, "oppositeDirection" : true, "depth" : 11 * mm});
        }
    });
